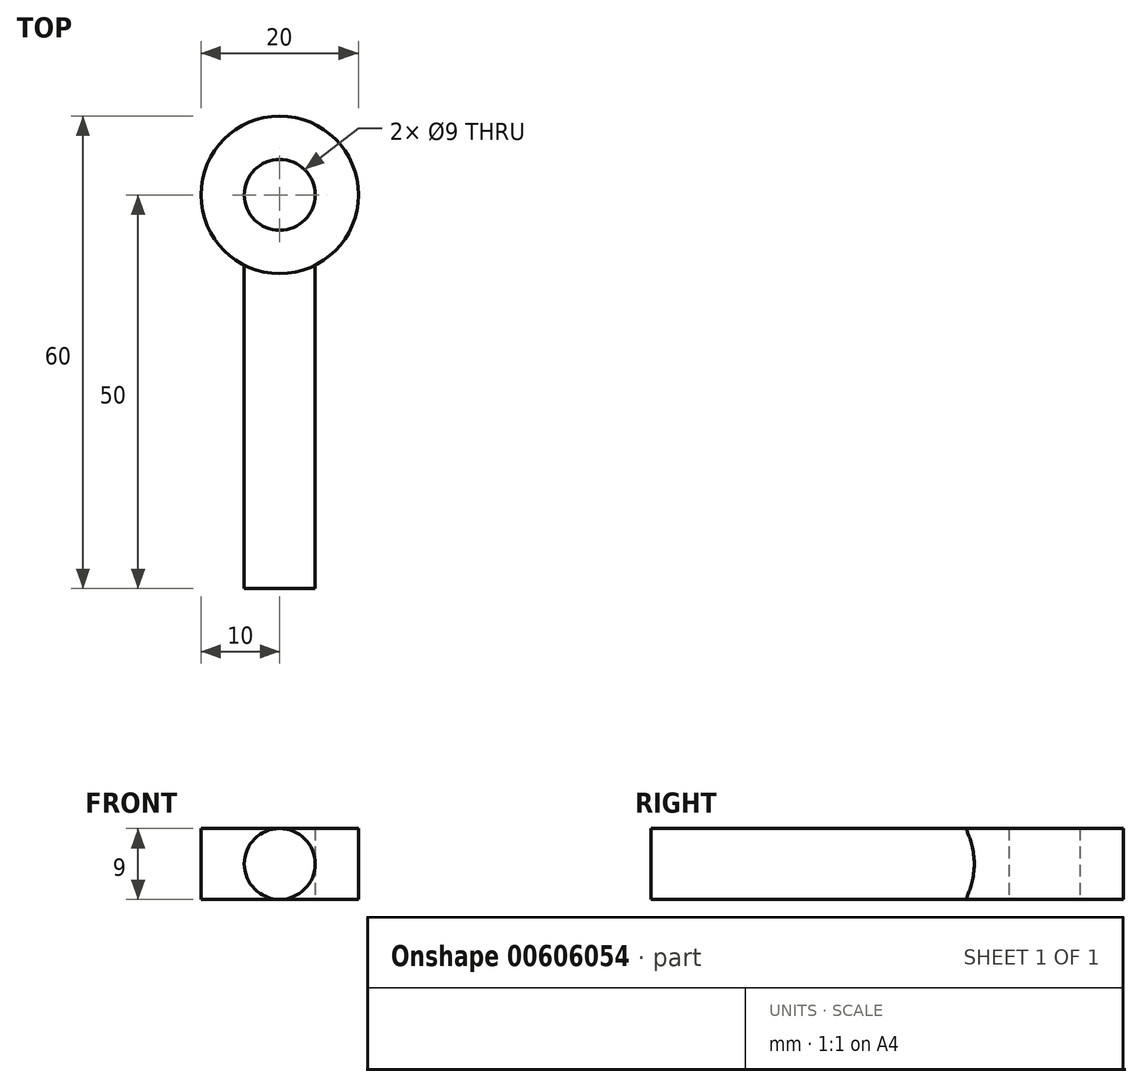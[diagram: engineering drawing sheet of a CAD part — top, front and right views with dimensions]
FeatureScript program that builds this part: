
annotation { "Feature Type Name" : "Feature", "Feature Type Description" : "" }
export const myFeature = defineFeature(function(context is Context, id is Id, definition is map)
    precondition{}
    {
        {
            var Q0;
            Q0=qCreatedBy(makeId("Top.planeOp"),FACE);
            var sketch = newSketch(context, id + "F0", { "sketchPlane" : qUnion([Q0])});
            skCircle(sketch, "E0", {"center": v(0, 0) * mm, "radius": 10 * mm});
            skCircle(sketch, "E1", {"center": v(0, 0) * mm, "radius": 4.5 * mm});
            skLineSegment(sketch, "E2", {"start": v(-4.5, 0) * mm, "end": v(-4.5, -50) * mm});
            skLineSegment(sketch, "E3", {"start": v(4.5, 0) * mm, "end": v(4.5, -50) * mm});
            skLineSegment(sketch, "E4", {"start": v(4.5, -50) * mm, "end": v(-4.5, -50) * mm});
            skSolve(sketch);
        }
        {
            var Q0;
            Q0 = qSketchRegion(id + "F0", true);
            extrude(context, id + "F1", {"entities" : qUnion([Q0]), "depth" : 9 * mm, "offsetDistance" : 25 * mm});
        }
        {
            var Q0;
            Q0=makeQuery(id+"F1.opExtrude","CAP_EDGE",EDGE,{"disambiguationData":[OSD([sQuery(id+"F0.wireOp",EDGE,"E2")])],"isStart":false});
            var Q1;
            Q1=makeQuery(id+"F1.opExtrude","CAP_EDGE",EDGE,{"disambiguationData":[OSD([sQuery(id+"F0.wireOp",EDGE,"E3")])],"isStart":false});
            var Q2;
            Q2=makeQuery(id+"F1.opExtrude","CAP_EDGE",EDGE,{"disambiguationData":[OSD([sQuery(id+"F0.wireOp",EDGE,"E3")])],"isStart":true});
            var Q3;
            Q3=makeQuery(id+"F1.opExtrude","CAP_EDGE",EDGE,{"disambiguationData":[OSD([sQuery(id+"F0.wireOp",EDGE,"E2")])],"isStart":true});
            fillet(context, id + "F2", {"entities" : qUnion([Q0, Q1, Q2, Q3]), "radius" : 4.5 * mm, "tangentPropagation" : true, "allowEdgeOverflow" : false});
        }
    });
